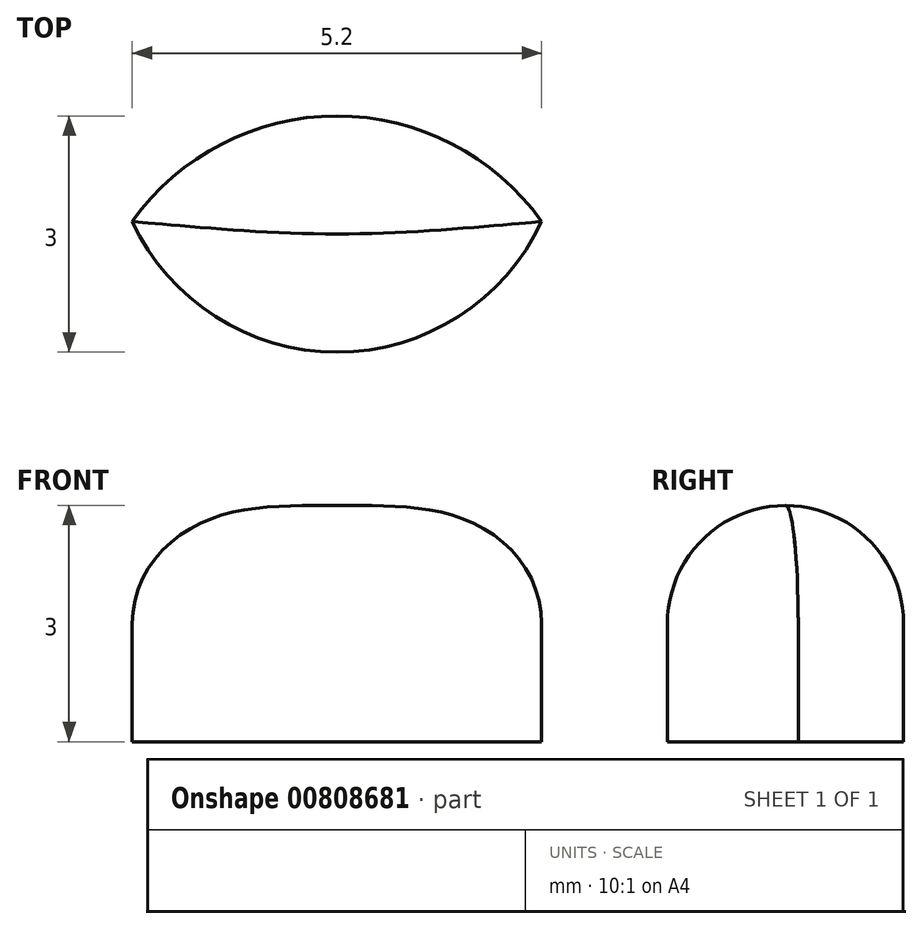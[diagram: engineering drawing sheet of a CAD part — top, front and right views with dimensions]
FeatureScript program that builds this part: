
annotation { "Feature Type Name" : "Feature", "Feature Type Description" : "" }
export const myFeature = defineFeature(function(context is Context, id is Id, definition is map)
    precondition{}
    {
        {
            var Q0;
            Q0=qCreatedBy(makeId("Top.planeOp"),FACE);
            var sketch = newSketch(context, id + "F0", { "sketchPlane" : qUnion([Q0])});
            skArc(sketch, "E0", {"start": v(2.87, 0) * mm, "mid": v(0.27, 1.34) * mm, "end": v(-2.33, 0) * mm});
            skArc(sketch, "E1", {"start": v(-2.33, 0) * mm, "mid": v(0.27, -1.66) * mm, "end": v(2.87, 0) * mm});
            skSolve(sketch);
        }
        {
            var Q0;
            Q0 = qSketchRegion(id + "F0", true);
            extrude(context, id + "F1", {"entities" : qUnion([Q0]), "depth" : 3 * mm, "offsetDistance" : 25 * mm});
        }
        {
            var Q0;
            Q0=makeQuery(id+"F1.opExtrude","CAP_EDGE",EDGE,{"disambiguationData":[OSD([sQuery(id+"F0.wireOp",EDGE,"E0")])],"isStart":false});
            var Q1;
            Q1=makeQuery(id+"F1.opExtrude","CAP_EDGE",EDGE,{"disambiguationData":[OSD([sQuery(id+"F0.wireOp",EDGE,"E1")])],"isStart":false});
            fillet(context, id + "F2", {"entities" : qUnion([Q0, Q1]), "radius" : 1.5 * mm, "tangentPropagation" : true, "allowEdgeOverflow" : false});
        }
    });
